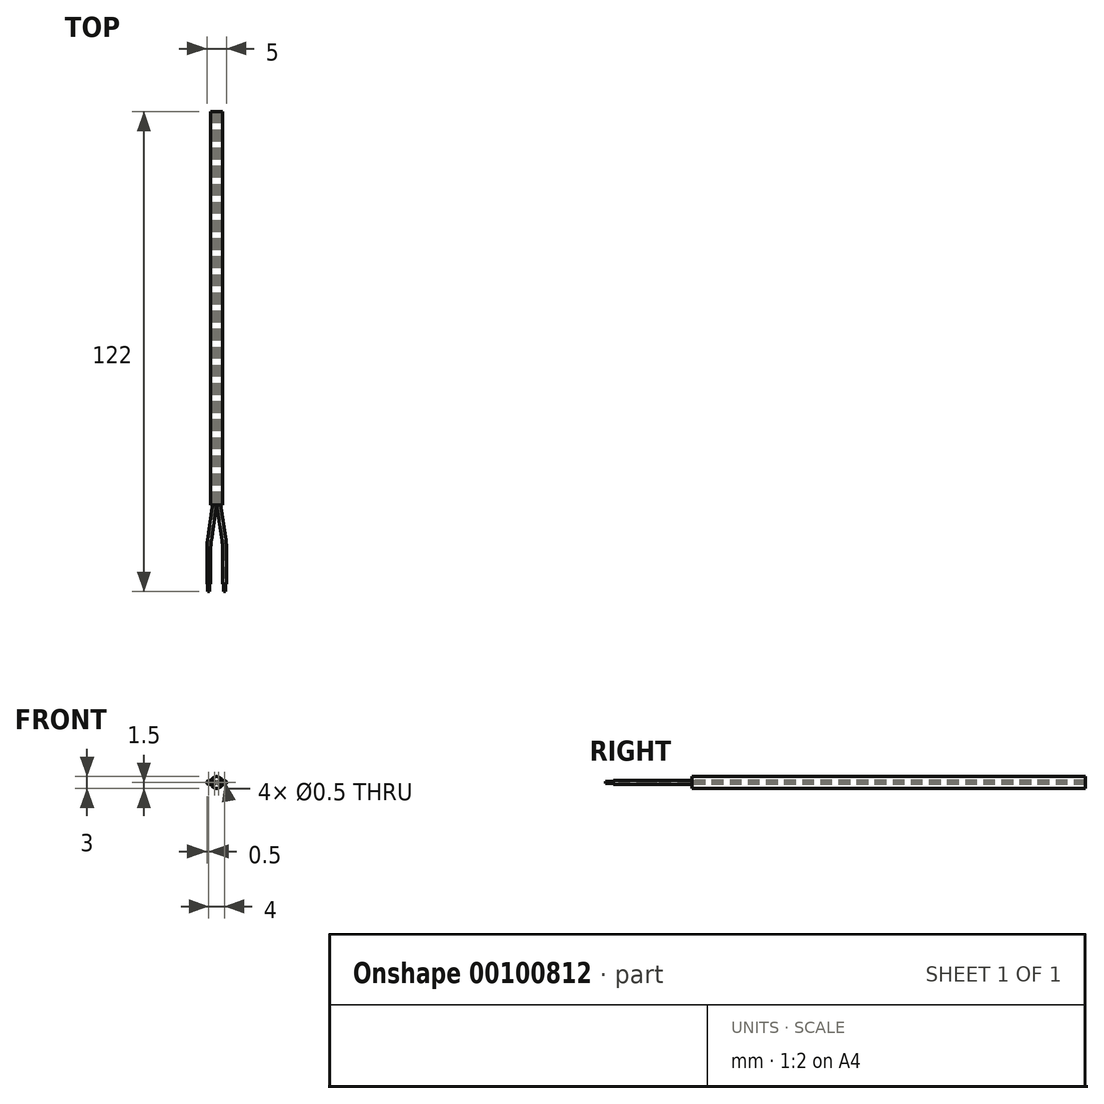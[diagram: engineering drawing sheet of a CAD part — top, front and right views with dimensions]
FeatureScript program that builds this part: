
annotation { "Feature Type Name" : "Feature", "Feature Type Description" : "" }
export const myFeature = defineFeature(function(context is Context, id is Id, definition is map)
    precondition{}
    {
        {
            var Q0;
            Q0=qCreatedBy(makeId("Front.planeOp"),FACE);
            var sketch = newSketch(context, id + "F0", { "sketchPlane" : qUnion([Q0])});
            skCircle(sketch, "E0", {"center": v(0, 0) * mm, "radius": 1.5 * mm});
            skCircle(sketch, "E1", {"center": v(0.5, 0) * mm, "radius": 0.5 * mm});
            skCircle(sketch, "E2", {"center": v(0.5, 0) * mm, "radius": 0.25 * mm});
            skCircle(sketch, "E3", {"center": v(-0.5, 0) * mm, "radius": 0.5 * mm});
            skCircle(sketch, "E4", {"center": v(-0.5, 0) * mm, "radius": 0.25 * mm});
            skSolve(sketch);
        }
        {
            var Q0;
            Q0=makeQuery(id+"F0.imprint","IMPRINT",FACE,{"disambiguationData":[TD([[makeQuery(id+"F0.imprint","IMPRINT",EDGE,{"derivedFrom":sQuery(id+"F0.wireOp",EDGE,"E0")}),1.0]])]});
            var Q1;
            Q1=makeQuery(id+"F0.imprint","IMPRINT",FACE,{"disambiguationData":[TD([[makeQuery(id+"F0.imprint","IMPRINT",EDGE,{"derivedFrom":sQuery(id+"F0.wireOp",EDGE,"E3")}),1.0]])]});
            var Q2;
            Q2=makeQuery(id+"F0.imprint","IMPRINT",FACE,{"disambiguationData":[TD([[makeQuery(id+"F0.imprint","IMPRINT",EDGE,{"derivedFrom":sQuery(id+"F0.wireOp",EDGE,"E4")}),1.0]])]});
            var Q3;
            Q3=makeQuery(id+"F0.imprint","IMPRINT",FACE,{"disambiguationData":[TD([[makeQuery(id+"F0.imprint","IMPRINT",EDGE,{"derivedFrom":sQuery(id+"F0.wireOp",EDGE,"E2")}),1.0]])]});
            var Q4;
            Q4=makeQuery(id+"F0.imprint","IMPRINT",FACE,{"disambiguationData":[TD([[makeQuery(id+"F0.imprint","IMPRINT",EDGE,{"derivedFrom":sQuery(id+"F0.wireOp",EDGE,"E1")}),1.0]])]});
            extrude(context, id + "F1", {"entities" : qUnion([Q0, Q1, Q2, Q3, Q4]), "depth" : 100 * mm});
        }
        {
            var Q0;
            Q0=qCreatedBy(makeId("Top.planeOp"),FACE);
            var sketch = newSketch(context, id + "F2", { "sketchPlane" : qUnion([Q0])});
            skLineSegment(sketch, "E5", {"start": v(0.5, 0) * mm, "end": v(0.5, -99.25) * mm});
            skLineSegment(sketch, "E6", {"start": v(0.61, -100.74) * mm, "end": v(1.83, -108.9) * mm});
            skLineSegment(sketch, "E7", {"start": v(2, -111.12) * mm, "end": v(2, -120) * mm});
            skPoint(sketch, "E8.visualSharp", {"position": v(0.5, -100) * mm});
            skArc(sketch, "E8.filletArc", {"start": v(0.5, -99.25) * mm, "mid": v(0.53, -100) * mm, "end": v(0.61, -100.74) * mm});
            skPoint(sketch, "E9.visualSharp", {"position": v(2, -110) * mm});
            skArc(sketch, "E9.filletArc", {"start": v(2, -111.12) * mm, "mid": v(1.96, -110) * mm, "end": v(1.83, -108.9) * mm});
            skLineSegment(sketch, "E10", {"start": v(2, -120) * mm, "end": v(2, -122) * mm});
            skArc(sketch, "E11.MirrorCS", {"start": v(-2, -111.12) * mm, "mid": v(-1.96, -110) * mm, "end": v(-1.83, -108.9) * mm});
            skArc(sketch, "E12.MirrorCS", {"start": v(-0.5, -99.25) * mm, "mid": v(-0.53, -100) * mm, "end": v(-0.61, -100.74) * mm});
            skLineSegment(sketch, "E13.MirrorCS", {"start": v(-2, -111.12) * mm, "end": v(-2, -120) * mm});
            skLineSegment(sketch, "E14.MirrorCS", {"start": v(-2, -120) * mm, "end": v(-2, -122) * mm});
            skPoint(sketch, "E15.MirrorP", {"position": v(-2, -110) * mm});
            skLineSegment(sketch, "E16.MirrorCS", {"start": v(-0.61, -100.74) * mm, "end": v(-1.83, -108.9) * mm});
            skLineSegment(sketch, "E17.MirrorCS", {"start": v(-0.5, 0) * mm, "end": v(-0.5, -99.25) * mm});
            skPoint(sketch, "E18.MirrorP", {"position": v(-0.5, -100) * mm});
            skSolve(sketch);
        }
        {
            var Q0;
            Q0=makeQuery(id+"F0.imprint","IMPRINT",FACE,{"disambiguationData":[TD([[makeQuery(id+"F0.imprint","IMPRINT",EDGE,{"derivedFrom":sQuery(id+"F0.wireOp",EDGE,"E2")}),1.0]])]});
            var Q1;
            Q1=sQuery(id+"F2.wireOp",EDGE,"E6");
            var Q2;
            Q2=sQuery(id+"F2.wireOp",EDGE,"E9.filletArc");
            var Q3;
            Q3=sQuery(id+"F2.wireOp",EDGE,"E7");
            var Q4;
            Q4=sQuery(id+"F2.wireOp",EDGE,"E8.filletArc");
            var Q5;
            Q5=sQuery(id+"F2.wireOp",EDGE,"E5");
            var Q6;
            Q6=sQuery(id+"F2.wireOp",EDGE,"E10");
            sweep(context, id + "F3", {"profiles" : qUnion([Q0]), "path" : qUnion([Q1, Q2, Q3, Q4, Q5, Q6])});
        }
        {
            var Q0;
            Q0=makeQuery(id+"F0.imprint","IMPRINT",FACE,{"disambiguationData":[TD([[makeQuery(id+"F0.imprint","IMPRINT",EDGE,{"derivedFrom":sQuery(id+"F0.wireOp",EDGE,"E4")}),1.0]])]});
            var Q1;
            Q1=sQuery(id+"F2.wireOp",EDGE,"E14.MirrorCS");
            var Q2;
            Q2=sQuery(id+"F2.wireOp",EDGE,"E13.MirrorCS");
            var Q3;
            Q3=sQuery(id+"F2.wireOp",EDGE,"E11.MirrorCS");
            var Q4;
            Q4=sQuery(id+"F2.wireOp",EDGE,"E16.MirrorCS");
            var Q5;
            Q5=sQuery(id+"F2.wireOp",EDGE,"E17.MirrorCS");
            var Q6;
            Q6=sQuery(id+"F2.wireOp",EDGE,"E12.MirrorCS");
            sweep(context, id + "F4", {"profiles" : qUnion([Q0]), "path" : qUnion([Q1, Q2, Q3, Q4, Q5, Q6])});
        }
        {
            var Q0;
            Q0=makeQuery(id+"F0.imprint","IMPRINT",FACE,{"disambiguationData":[TD([[makeQuery(id+"F0.imprint","IMPRINT",EDGE,{"derivedFrom":sQuery(id+"F0.wireOp",EDGE,"E1")}),1.0]])]});
            var Q1;
            Q1=sQuery(id+"F2.wireOp",EDGE,"E5");
            var Q2;
            Q2=sQuery(id+"F2.wireOp",EDGE,"E8.filletArc");
            var Q3;
            Q3=sQuery(id+"F2.wireOp",EDGE,"E6");
            var Q4;
            Q4=sQuery(id+"F2.wireOp",EDGE,"E9.filletArc");
            var Q5;
            Q5=sQuery(id+"F2.wireOp",EDGE,"E7");
            sweep(context, id + "F5", {"profiles" : qUnion([Q0]), "path" : qUnion([Q1, Q2, Q3, Q4, Q5])});
        }
        {
            var Q0;
            Q0=makeQuery(id+"F0.imprint","IMPRINT",FACE,{"disambiguationData":[TD([[makeQuery(id+"F0.imprint","IMPRINT",EDGE,{"derivedFrom":sQuery(id+"F0.wireOp",EDGE,"E3")}),1.0]])]});
            var Q1;
            Q1=sQuery(id+"F2.wireOp",EDGE,"E13.MirrorCS");
            var Q2;
            Q2=sQuery(id+"F2.wireOp",EDGE,"E11.MirrorCS");
            var Q3;
            Q3=sQuery(id+"F2.wireOp",EDGE,"E16.MirrorCS");
            var Q4;
            Q4=sQuery(id+"F2.wireOp",EDGE,"E12.MirrorCS");
            var Q5;
            Q5=sQuery(id+"F2.wireOp",EDGE,"E17.MirrorCS");
            sweep(context, id + "F6", {"profiles" : qUnion([Q0]), "path" : qUnion([Q1, Q2, Q3, Q4, Q5])});
        }
    });
